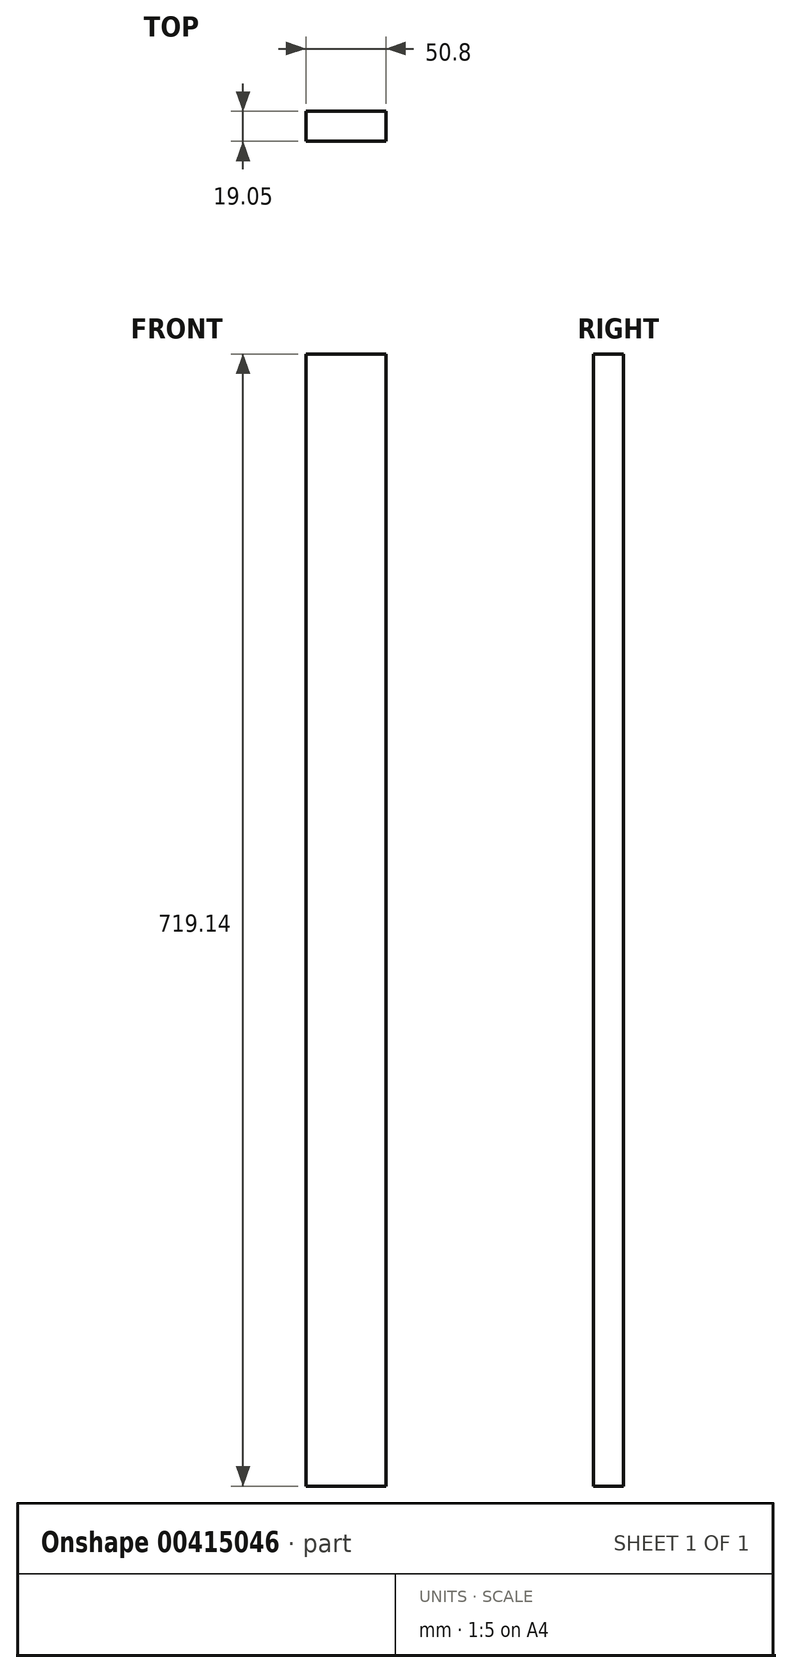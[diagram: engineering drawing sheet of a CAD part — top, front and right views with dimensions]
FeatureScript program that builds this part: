
annotation { "Feature Type Name" : "Feature", "Feature Type Description" : "" }
export const myFeature = defineFeature(function(context is Context, id is Id, definition is map)
    precondition{}
    {
        {
            var Q0;
            Q0=qCreatedBy(makeId("Front.planeOp"),FACE);
            var sketch = newSketch(context, id + "F0", { "sketchPlane" : qUnion([Q0])});
            skLineSegment(sketch, "E0.bottom", {"start": v(0, 0) * mm, "end": v(50.8, 0) * mm});
            skLineSegment(sketch, "E0.top", {"start": v(0, 719.14) * mm, "end": v(50.8, 719.14) * mm});
            skLineSegment(sketch, "E0.left", {"start": v(0, 0) * mm, "end": v(0, 719.14) * mm});
            skLineSegment(sketch, "E0.right", {"start": v(50.8, 0) * mm, "end": v(50.8, 719.14) * mm});
            skSolve(sketch);
        }
        {
            var Q0;
            Q0=makeQuery(id+"F0.imprint","IMPRINT",FACE,{"disambiguationData":[TD([[makeQuery(id+"F0.imprint","IMPRINT",EDGE,{"derivedFrom":sQuery(id+"F0.wireOp",EDGE,"E0.bottom")}),1.0]])]});
            extrude(context, id + "F1", {"entities" : qUnion([Q0]), "depth" : 19.05 * mm, "offsetDistance" : 25.4 * mm});
        }
    });
